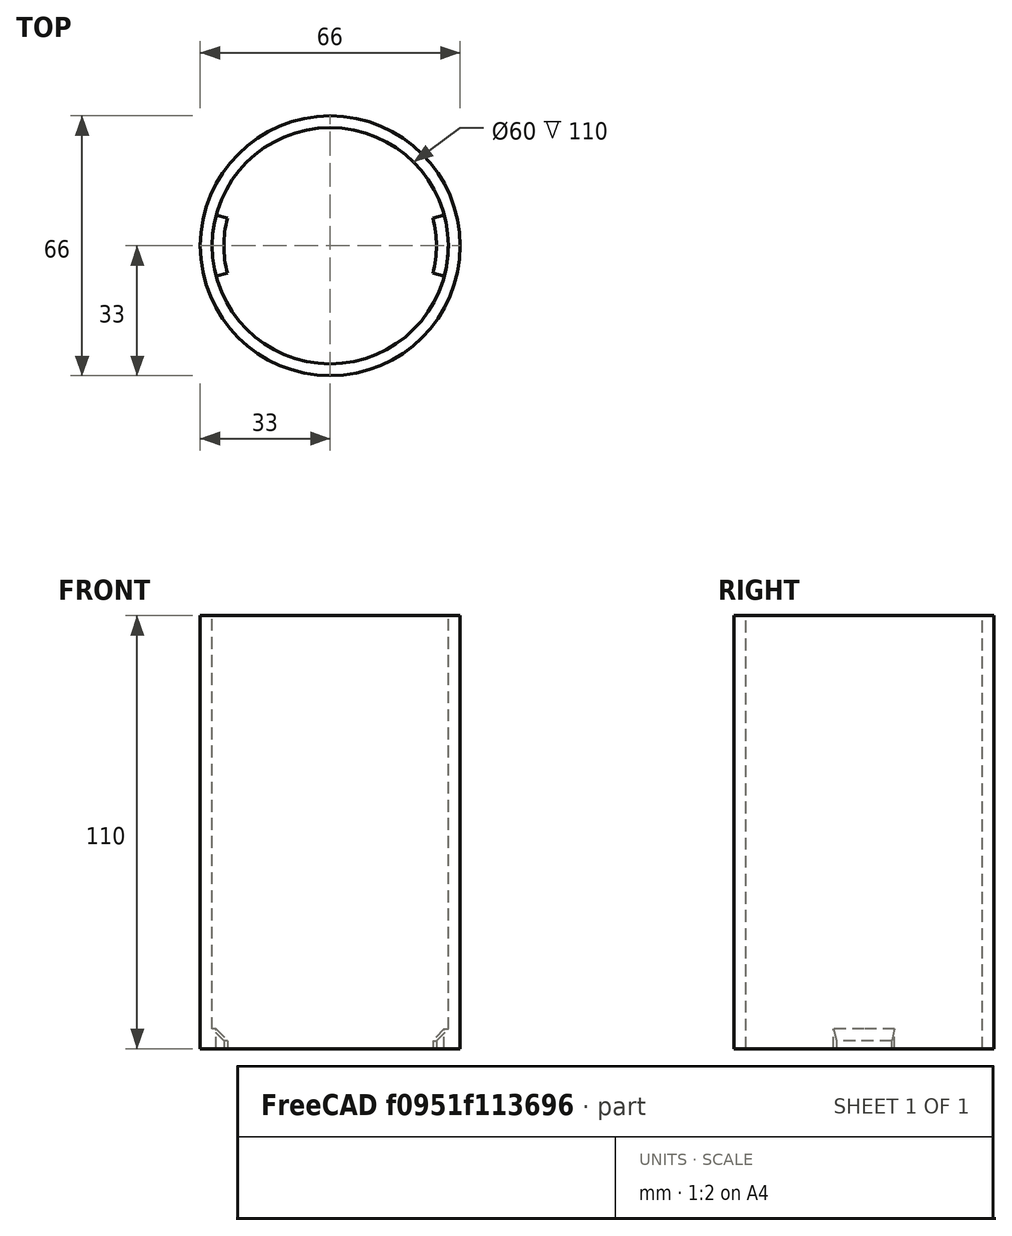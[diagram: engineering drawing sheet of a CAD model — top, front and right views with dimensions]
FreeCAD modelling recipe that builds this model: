
FCSTD DOCUMENT  (FreeCAD 1.0R39319 (Git))
Label: 露营灯
License: All rights reserved
LicenseURL: https://en.wikipedia.org/wiki/All_rights_reserved
objects: Sketcher::SketchObject×2, PartDesign::Revolution×2, Assembly::JointGroup×1, Assembly::AssemblyObject×1, PartDesign::Mirrored×1, PartDesign::PolarPattern×1, PartDesign::Body×1
note: 15 computed .brp shape members not serialized (recipe doc carries the construction recipe); baked Part::Feature solids carry a one-line shape summary decoded from their .brp

FEATURE [Assembly::JointGroup] Joints
FEATURE [Assembly::AssemblyObject] Assembly  label="提灯"
  Group = -> [Joints]
  Origin = -> Origin
  Type = Assembly
FEATURE [Sketcher::SketchObject] Sketch
  ArcFitTolerance = 1e-06
  AttachmentSupport = -> [XZ_Plane001]
  FullyConstrained = true
  MakeInternals = false
  MapMode = 5
  Placement = pos=(0,0,0) rot=(1,0,0;1.5708rad)
  sketch-geometry (4):
    g0: LineSegment StartX=-30 StartY=0 StartZ=0 EndX=-33 EndY=0 EndZ=0
    g1: LineSegment StartX=-33 StartY=0 StartZ=0 EndX=-33 EndY=-55 EndZ=0
    g2: LineSegment StartX=-33 StartY=-55 StartZ=0 EndX=-30 EndY=-55 EndZ=0
    g3: LineSegment StartX=-30 StartY=-55 StartZ=0 EndX=-30 EndY=0 EndZ=0
  constraints (12):
    c: Coincident(g0,g1)
    c: Coincident(g1,g2)
    c: Coincident(g2,g3)
    c: Coincident(g3,g0)
    c: Horizontal(g0)
    c: Horizontal(g2)
    c: Vertical(g1)
    c: Vertical(g3)
    c: PointOnObject(g0,g-1)
    c: Distance(g-2,g3) = 30
    c: DistanceX(g2,g2) = 3
    c: DistanceY(g1,g1) = 55
FEATURE [PartDesign::Revolution] Revolution
  Angle = 360
  Angle2 = 60
  Axis = (0,2e-16,1)
  Base = (0,0,0)
  Placement = pos=(0,0,0) rot=(1,0,0;1.5708rad)
  Profile = -> Sketch
  ReferenceAxis = -> Sketch [V_Axis]
  Refine = true
  Suppressed = false
  Type = 0
FEATURE [PartDesign::Mirrored] Mirrored
  BaseFeature = -> Revolution
  MirrorPlane = -> XY_Plane001
  Placement = pos=(0,0,0) rot=(1,0,0;1.5708rad)
  Refine = true
  Suppressed = false
  TransformMode = 1
FEATURE [Sketcher::SketchObject] Sketch001
  ArcFitTolerance = 1e-06
  AttachmentSupport = -> [XZ_Plane001]
  FullyConstrained = true
  MakeInternals = false
  MapMode = 5
  Placement = pos=(0,0,0) rot=(1,0,0;1.5708rad)
  sketch-geometry (4):
    g0: LineSegment StartX=-27 StartY=-53 StartZ=0 EndX=-27 EndY=-55 EndZ=0
    g1: LineSegment StartX=-27 StartY=-55 StartZ=0 EndX=-30 EndY=-55 EndZ=0
    g2: LineSegment StartX=-30 StartY=-55 StartZ=0 EndX=-30 EndY=-50 EndZ=0
    g3: LineSegment StartX=-30 StartY=-50 StartZ=0 EndX=-27 EndY=-53 EndZ=0
  constraints (12):
    c: Vertical(g0)
    c: Coincident(g1,g0)
    c: Horizontal(g1)
    c: Coincident(g2,g1)
    c: Vertical(g2)
    c: Coincident(g3,g2)
    c: Coincident(g3,g0)
    c: DistanceX(g1,g1) = 3
    c: DistanceY(g0,g0) = 2
    c: DistanceY(g2,g2) = 5
    c: Distance(g-2,g2) = 30
    c: Distance(g2,g-1) = 50
FEATURE [PartDesign::Revolution] Revolution001
  Angle = 30
  Angle2 = 60
  Axis = (0,2e-16,1)
  Base = (0,0,0)
  BaseFeature = -> Mirrored
  Midplane = true
  Placement = pos=(0,0,0) rot=(1,0,0;1.5708rad)
  Profile = -> Sketch001
  ReferenceAxis = -> Sketch001 [V_Axis]
  Refine = true
  Suppressed = false
  Type = 0
FEATURE [PartDesign::PolarPattern] PolarPattern
  Angle = 360
  Axis = -> Z_Axis001
  BaseFeature = -> Revolution001
  Mode = 0
  Occurrences = 4
  Offset = 120
  Placement = pos=(0,0,0) rot=(1,0,0;1.5708rad)
  Refine = true
  Suppressed = false
  TransformMode = 1
FEATURE [PartDesign::Body] Body  label="灯罩"
  AllowCompound = true
  Group = -> [Sketch,Revolution,Mirrored,Sketch001,Revolution001,PolarPattern]
  Origin = -> Origin001
  Tip = -> PolarPattern
